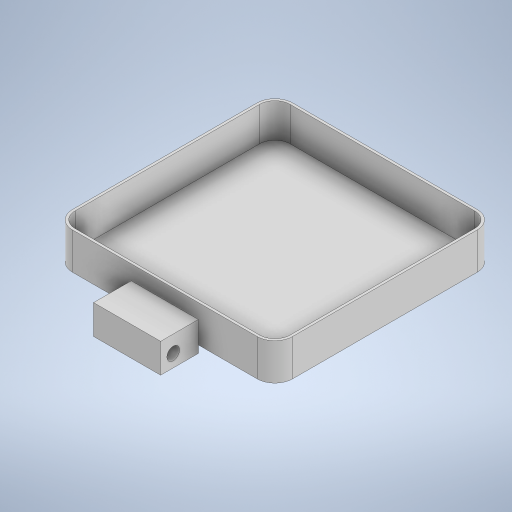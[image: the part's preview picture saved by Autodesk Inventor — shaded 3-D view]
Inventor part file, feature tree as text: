
AUTODESK INVENTOR PART (.ipt)
format: ipt  version: 2024 (Build 280153000, 153)  size: 280,576 bytes
history: native  units: mm
features: extrude x3, sketch x3, other x1, fillet x1, shell x1
ambient origin geometry x8: Origin, YZ Plane, XZ Plane, XY Plane, X Axis, Y Axis, Z Axis, Center Point
bodies: Body1 (feature_tree)
feature tree (9):
  other  "Bryła1"
  extrude  "Wyciągnięcie proste1"  Depth=105.0mm
  fillet  "Zaokrąglenie1"  Radius=105.0mm
  shell  "Skorupa1"  Thickness=52.5mm
  sketch  "Szkic4"
  extrude  "Wyciągnięcie proste4"  Depth=52.5mm
  extrude  "Wyciągnięcie proste6"  Depth=17.5mm TaperAngle=0.0deg
  sketch  "Szkic1"
  sketch  "Szkic6"
